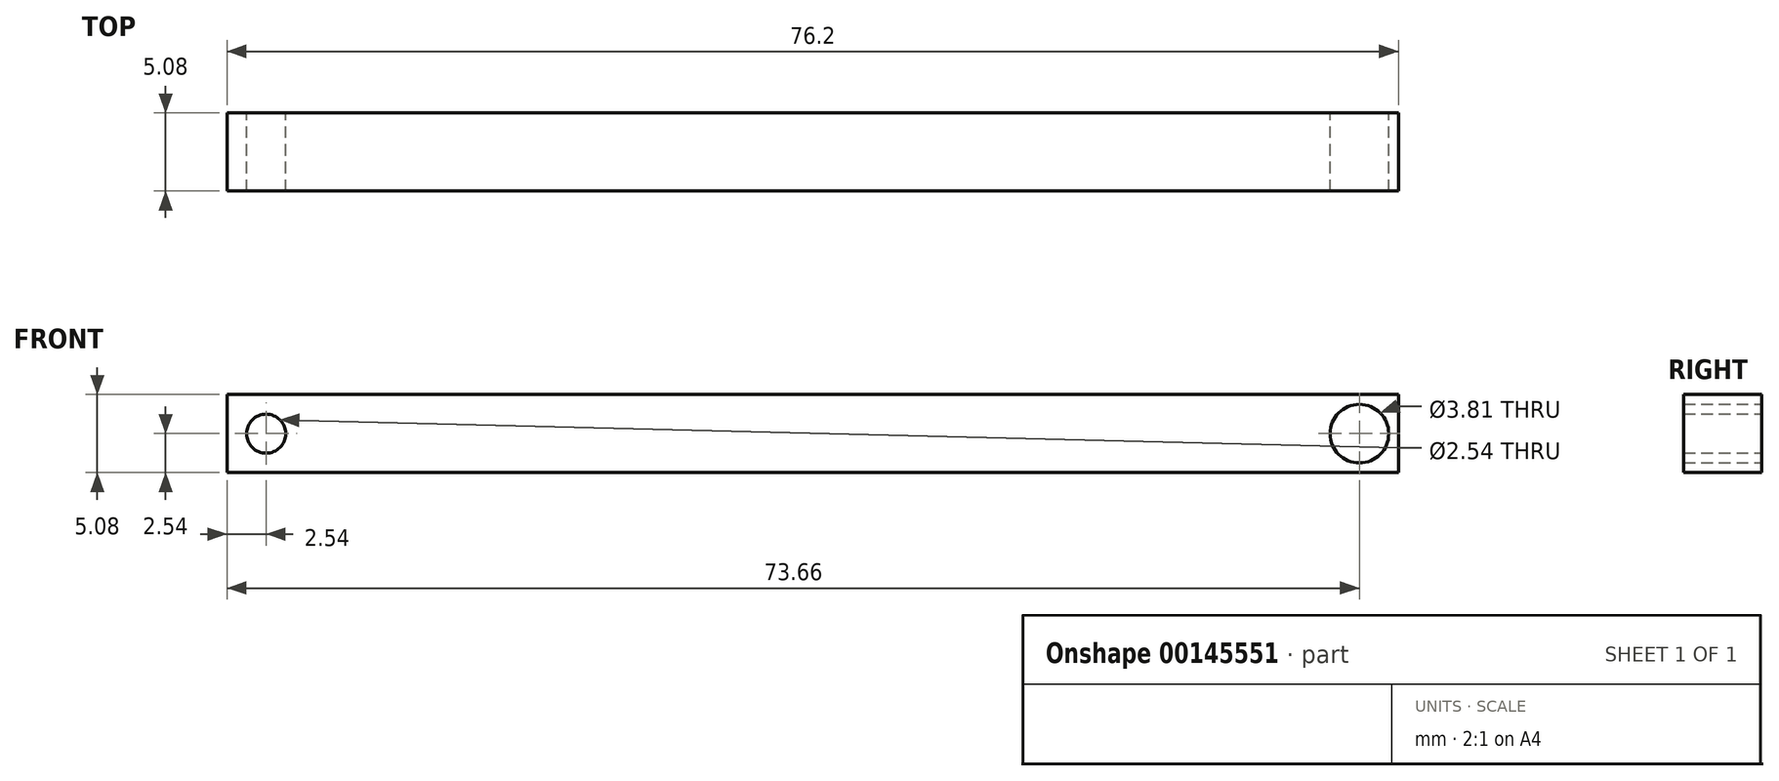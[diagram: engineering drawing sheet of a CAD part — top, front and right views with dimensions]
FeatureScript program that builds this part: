
annotation { "Feature Type Name" : "Feature", "Feature Type Description" : "" }
export const myFeature = defineFeature(function(context is Context, id is Id, definition is map)
    precondition{}
    {
        {
            var Q0;
            Q0=qCreatedBy(makeId("Front.planeOp"),FACE);
            var sketch = newSketch(context, id + "F0", { "sketchPlane" : qUnion([Q0])});
            skLineSegment(sketch, "E0.bottom", {"start": v(0, 0) * mm, "end": v(76.2, 0) * mm});
            skLineSegment(sketch, "E0.top", {"start": v(0, -5.08) * mm, "end": v(76.2, -5.08) * mm});
            skLineSegment(sketch, "E0.left", {"start": v(0, 0) * mm, "end": v(0, -5.08) * mm});
            skLineSegment(sketch, "E0.right", {"start": v(76.2, 0) * mm, "end": v(76.2, -5.08) * mm});
            skCircle(sketch, "E1", {"center": v(73.66, -2.54) * mm, "radius": 1.9 * mm});
            skCircle(sketch, "E2", {"center": v(2.54, -2.54) * mm, "radius": 1.27 * mm});
            skSolve(sketch);
        }
        {
            var Q0;
            Q0 = qSketchRegion(id + "F0", true);
            extrude(context, id + "F1", {"entities" : qUnion([Q0]), "depth" : 5.08 * mm});
        }
    });
